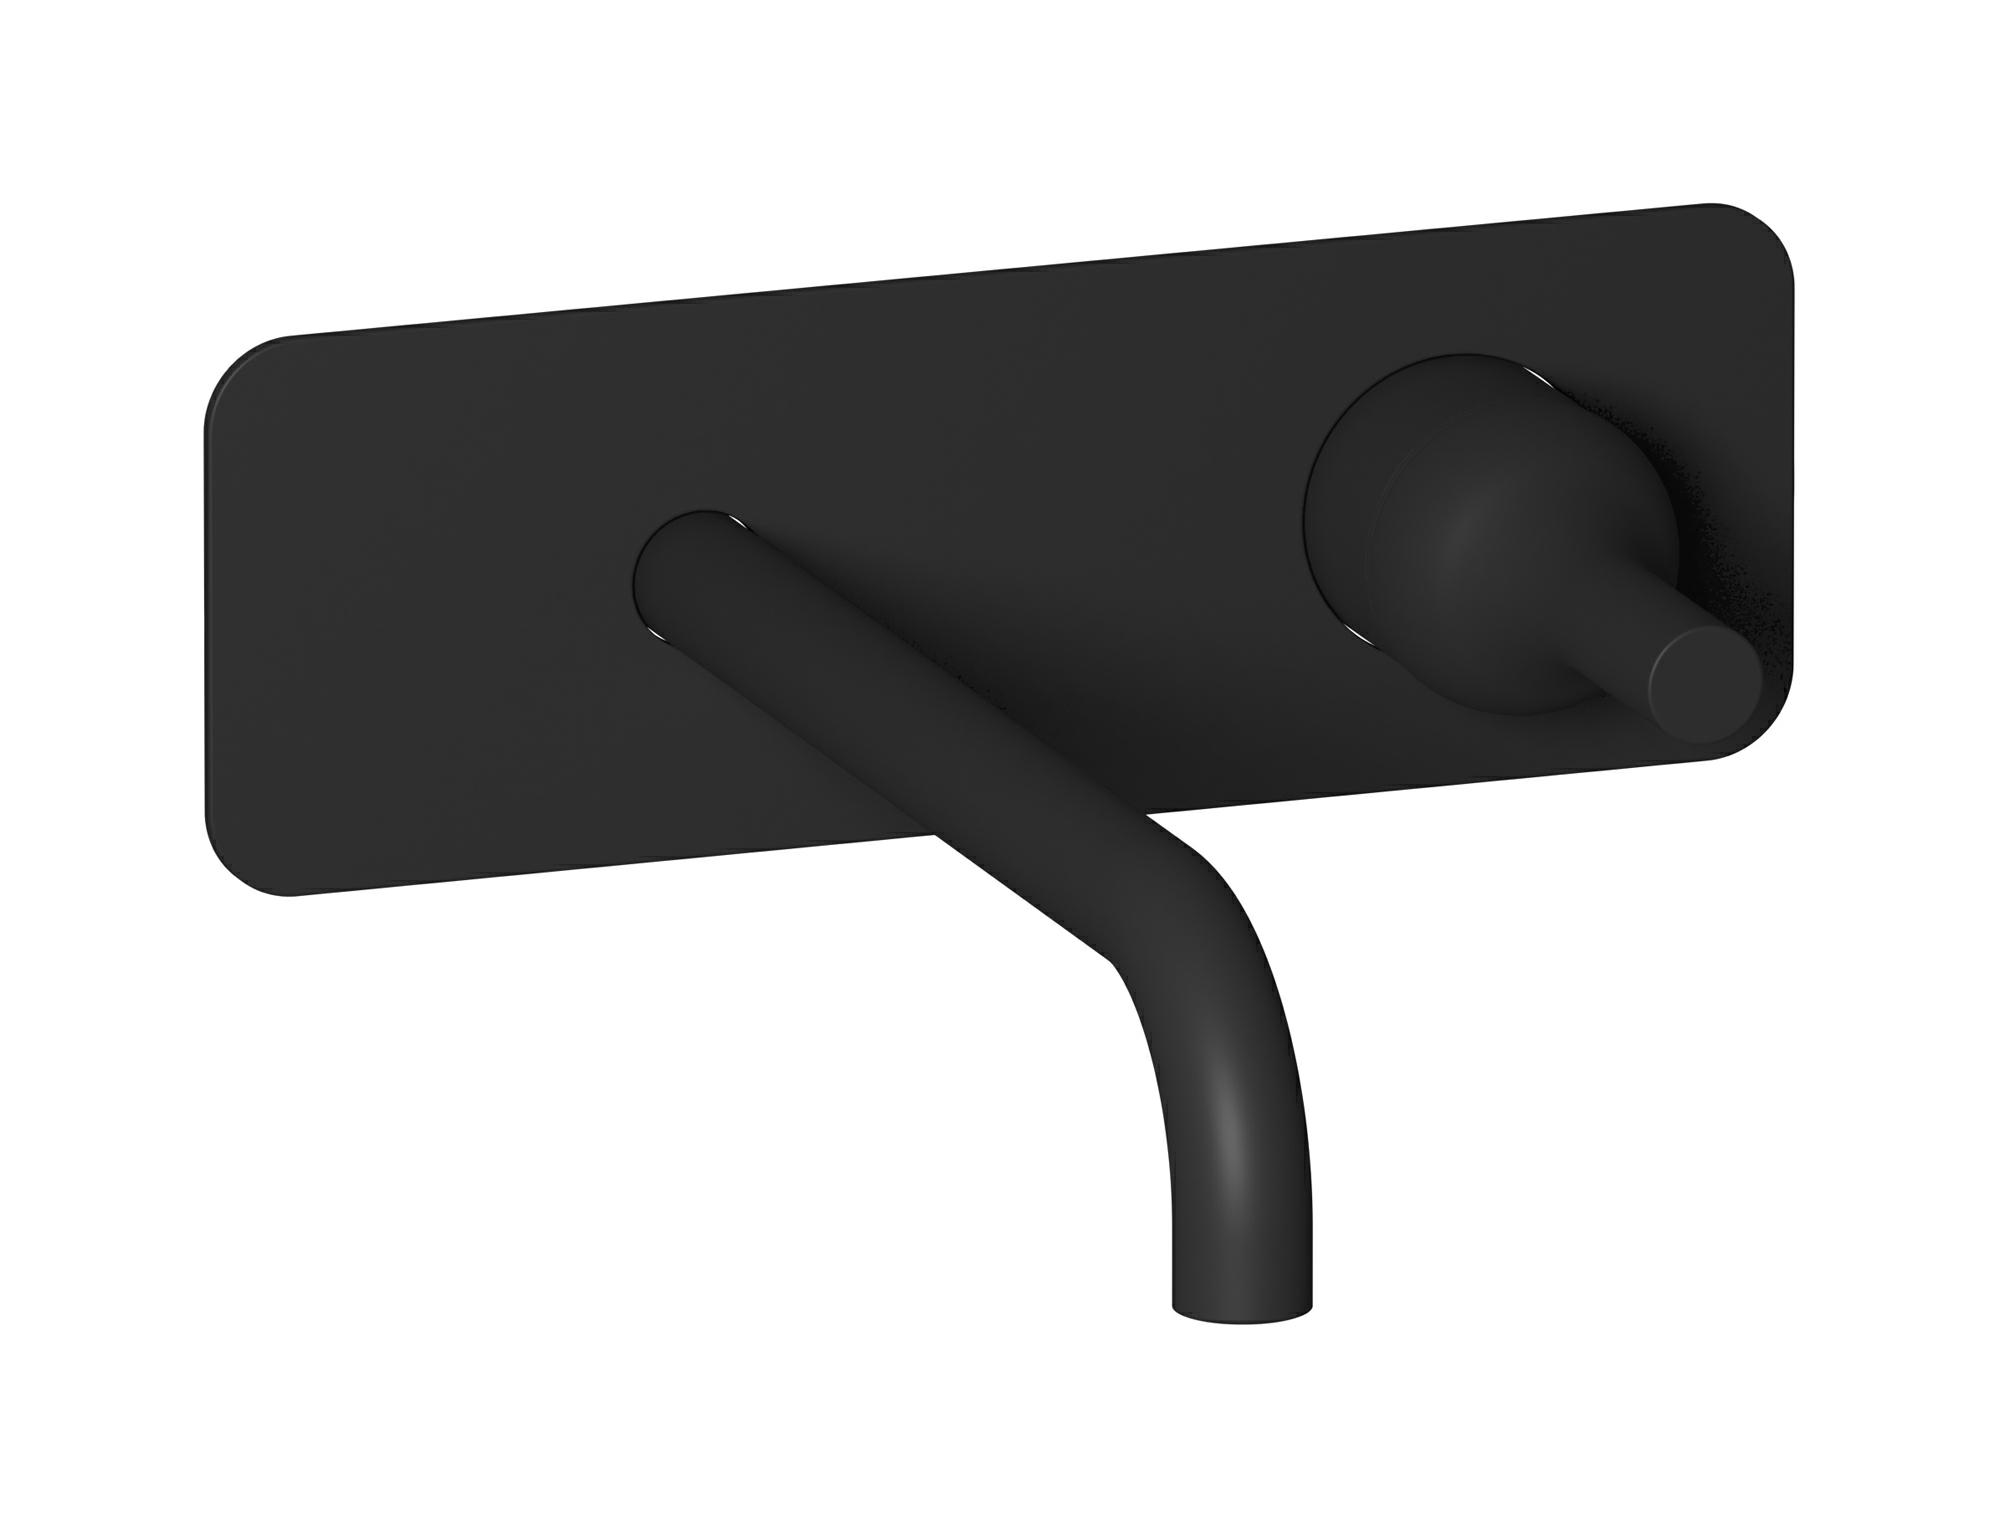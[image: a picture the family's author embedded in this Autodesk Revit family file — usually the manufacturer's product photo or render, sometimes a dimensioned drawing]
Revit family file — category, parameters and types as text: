
# Revit family: BI207
name_source: partatom
category: Apparecchi idraulici
units: mm (PartAtom-declared; Revit-internal decimal feet)

## family parameters
Basato su piano di lavoro = No
Condiviso = No
Mantieni orientamento annotazione = No
Numero OmniClass = 23.45.55.17
Punto di calcolo locali = No
Quota connettore circolare = Usa diametro
Sempre verticale = Sì
Taglio con vuoti quando caricato = No
Tipo di parte = Normale
Titolo OmniClass = Mixing Faucets

## types (4) — shared parameters
Cold water inlet = 10 mm  [stored 0.0328084 ft]
Commenti sul tipo = Wall mounted washbasin mixer with long spout complete with drain
Connessione CW = No
Connessione HW = No
Connessione di scarico = No
Connessione di ventilazione = No
Descrizione = Wall mounted washbasin mixer with long spout complete with drain
Hot water inlet = 10 mm  [stored 0.0328084 ft]
Produttore = IB Rubinetterie S.p.A.
URL = https://www.weareib.it
zero-valued in all types: Prospetto di default

## per-type parameters (varying)
| type | Finishes surface | Immagine tipo | Modello |
| Chrome | IB_Chrome | BI207CC.jpg | BI207CC |
| Matt White | IB_matt white | BI207BO.jpg | BI207BO |
| Matt Black | IB_matt black | BI207NP.jpg | BI207NP |
| Brushed Nickel | IB_Brushed nickel | BI207SS.jpg | BI207SS |

note: [stored X ft] marks values corroborated as IEEE doubles in the binary element streams (Revit-internal decimal feet)
